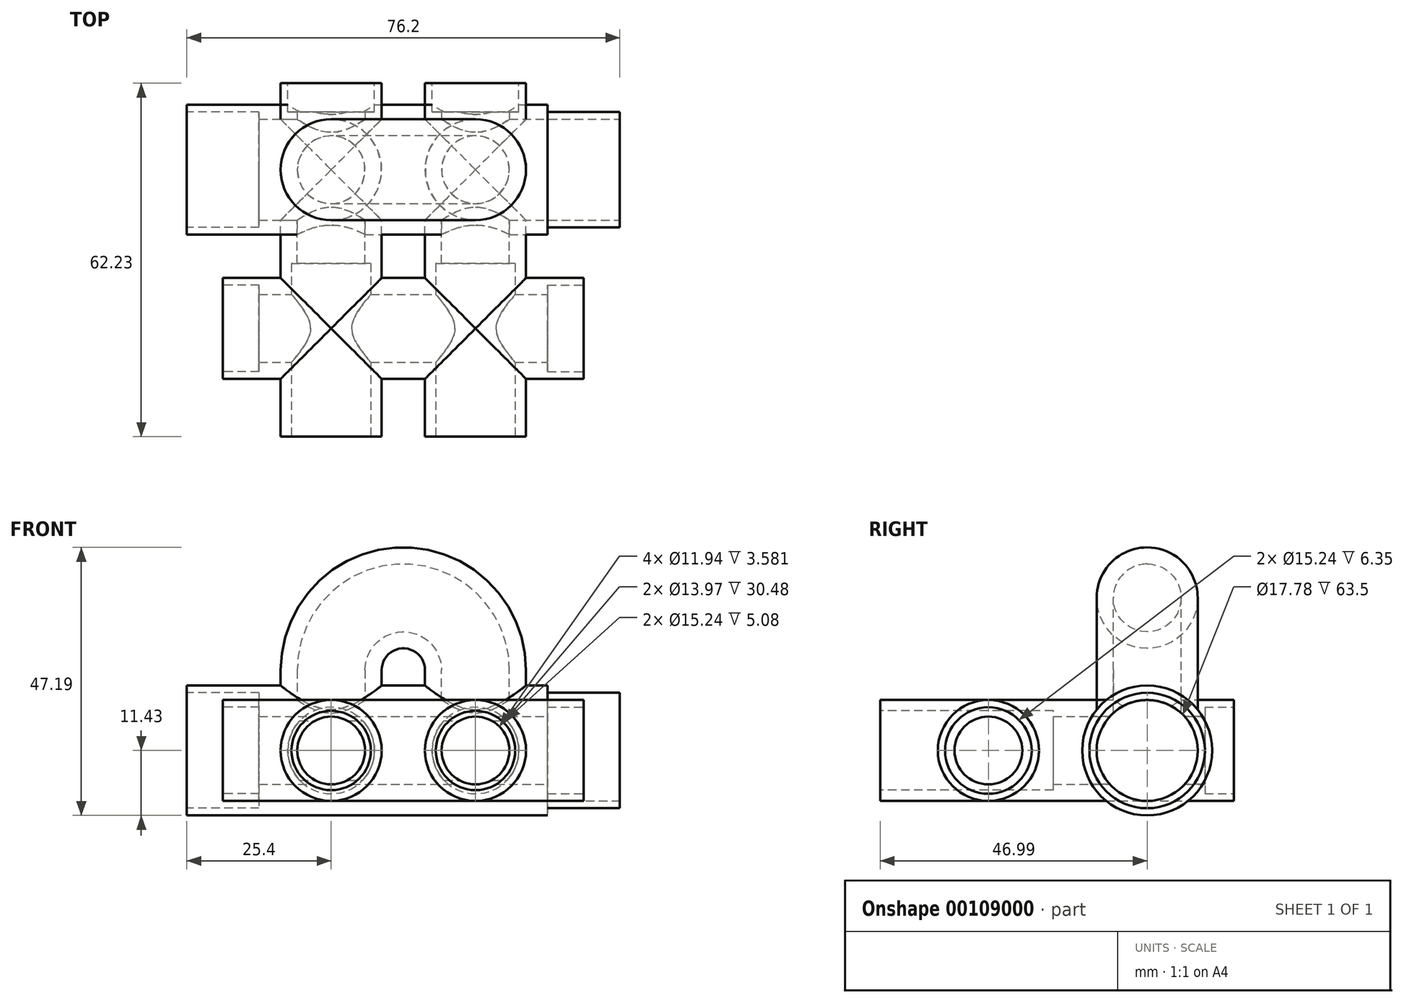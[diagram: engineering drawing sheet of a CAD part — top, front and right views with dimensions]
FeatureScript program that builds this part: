
annotation { "Feature Type Name" : "Feature", "Feature Type Description" : "" }
export const myFeature = defineFeature(function(context is Context, id is Id, definition is map)
    precondition{}
    {
        {
            var Q0;
            Q0=qCreatedBy(makeId("Top.planeOp"),FACE);
            var sketch = newSketch(context, id + "F0", { "sketchPlane" : qUnion([Q0])});
            skLineSegment(sketch, "E0", {"start": v(0, 0) * mm, "end": v(0, 27.94) * mm});
            skLineSegment(sketch, "E1", {"start": v(0, 27.94) * mm, "end": v(-25.4, 27.94) * mm});
            skLineSegment(sketch, "E2", {"start": v(-25.4, 27.94) * mm, "end": v(-25.4, 0) * mm});
            skLineSegment(sketch, "E3", {"start": v(0, 0) * mm, "end": v(0, 43.18) * mm});
            skPoint(sketch, "E3.endSnap0", {"position": v(0, 13.97) * mm});
            skLineSegment(sketch, "E4", {"start": v(-44.94, 0) * mm, "end": v(-34.3, 0) * mm});
            skArc(sketch, "E5", {"start": v(-34.3, 0) * mm, "mid": v(-28, 2.6) * mm, "end": v(-25.4, 8.9) * mm});
            skLineSegment(sketch, "E6", {"start": v(-25.4, 0) * mm, "end": v(0, 0) * mm});
            skLineSegment(sketch, "E7", {"start": v(-34.3, 0) * mm, "end": v(-25.4, 0) * mm});
            skLineSegment(sketch, "E8", {"start": v(-34.3, 0) * mm, "end": v(-34.3, 8.9) * mm});
            skLineSegment(sketch, "E9", {"start": v(-34.3, 8.9) * mm, "end": v(-25.4, 8.9) * mm});
            skSolve(sketch);
        }
        {
            var Q0;
            Q0=qCreatedBy(makeId("Front.planeOp"),FACE);
            var sketch = newSketch(context, id + "F1", { "sketchPlane" : qUnion([Q0])});
            skCircle(sketch, "E10", {"center": v(0, 0) * mm, "radius": 5.97 * mm});
            skCircle(sketch, "E11", {"center": v(0, 0) * mm, "radius": 8.9 * mm});
            skCircle(sketch, "E12", {"center": v(-25.4, 0) * mm, "radius": 5.97 * mm});
            skCircle(sketch, "E13", {"center": v(-25.4, 0) * mm, "radius": 8.9 * mm});
            skSolve(sketch);
        }
        {
            var Q0;
            Q0=qCreatedBy(makeId("Right.planeOp"),FACE);
            cPlane(context, id + "F2", {"entities" : qUnion([Q0]), "cplaneType" : CPlaneType.OFFSET, "offset" : 12.7 * mm, "width" : 152.4 * mm, "height" : 152.4 * mm});
        }
        {
            var Q0;
            Q0=qCreatedBy(id+"F2.planeOp",FACE);
            var sketch = newSketch(context, id + "F3", { "sketchPlane" : qUnion([Q0])});
            skCircle(sketch, "E14", {"center": v(27.94, 0) * mm, "radius": 8.9 * mm});
            skCircle(sketch, "E15", {"center": v(27.94, 0) * mm, "radius": 11.43 * mm});
            skSolve(sketch);
        }
        {
            var Q0;
            Q0=makeQuery(id+"F3.imprint","IMPRINT",FACE,{"disambiguationData":[TD([[makeQuery(id+"F3.imprint","IMPRINT",EDGE,{"derivedFrom":sQuery(id+"F3.wireOp",EDGE,"E14")}),-1.0]])]});
            extrude(context, id + "F4", {"entities" : qUnion([Q0]), "oppositeDirection" : true, "depth" : 63.5 * mm});
        }
        {
            var Q0;
            Q0=qCreatedBy(makeId("Front.planeOp"),FACE);
            cPlane(context, id + "F5", {"entities" : qUnion([Q0]), "cplaneType" : CPlaneType.OFFSET, "offset" : 27.94 * mm, "oppositeDirection" : true, "width" : 152.4 * mm, "height" : 152.4 * mm});
        }
        {
            var Q0;
            Q0=qCreatedBy(id+"F5.planeOp",FACE);
            var sketch = newSketch(context, id + "F6", { "sketchPlane" : qUnion([Q0])});
            skLineSegment(sketch, "E16", {"start": v(0, 0) * mm, "end": v(0, 14.17) * mm});
            skLineSegment(sketch, "E17", {"start": v(-25.4, 0) * mm, "end": v(-25.4, 14.17) * mm});
            skArc(sketch, "E18", {"start": v(-25.4, 14.17) * mm, "mid": v(-12.7, 26.87) * mm, "end": v(0, 14.17) * mm});
            skLineSegment(sketch, "E19", {"start": v(-25.4, 0) * mm, "end": v(-25.4, 8.9) * mm});
            skSolve(sketch);
        }
        {
            var Q0;
            Q0=qCreatedBy(makeId("Top.planeOp"),FACE);
            var sketch = newSketch(context, id + "F7", { "sketchPlane" : qUnion([Q0])});
            skCircle(sketch, "E20", {"center": v(0, 27.94) * mm, "radius": 5.97 * mm});
            skCircle(sketch, "E21", {"center": v(0, 27.94) * mm, "radius": 8.9 * mm});
            skSolve(sketch);
        }
        {
            var Q0;
            Q0=makeQuery(id+"F7.imprint","IMPRINT",FACE,{"disambiguationData":[TD([[makeQuery(id+"F7.imprint","IMPRINT",EDGE,{"derivedFrom":sQuery(id+"F7.wireOp",EDGE,"E20")}),-1.0]])]});
            var Q1;
            Q1=sQuery(id+"F6.wireOp",EDGE,"E16");
            var Q2;
            Q2=sQuery(id+"F6.wireOp",EDGE,"E18");
            var Q3;
            Q3=sQuery(id+"F6.wireOp",EDGE,"E17");
            sweep(context, id + "F8", {"operationType" : NewBodyOperationType.ADD, "profiles" : qUnion([Q0]), "path" : qUnion([Q1, Q2, Q3])});
        }
        {
            var Q0;
            Q0=makeQuery(id+"F1.imprint","IMPRINT",FACE,{"disambiguationData":[TD([[makeQuery(id+"F1.imprint","IMPRINT",EDGE,{"derivedFrom":sQuery(id+"F1.wireOp",EDGE,"E10")}),-1.0]])]});
            var Q1;
            Q1=makeQuery(id+"F1.imprint","IMPRINT",FACE,{"disambiguationData":[TD([[makeQuery(id+"F1.imprint","IMPRINT",EDGE,{"derivedFrom":sQuery(id+"F1.wireOp",EDGE,"E12")}),-1.0]])]});
            var Q2;
            Q2=sQuery(id+"F0.wireOp",EDGE,"E3");
            sweep(context, id + "F9", {"profiles" : qUnion([Q0, Q1]), "path" : qUnion([Q2])});
        }
        {
            var Q0;
            Q0=makeQuery(id+"F3.imprint","IMPRINT",FACE,{"disambiguationData":[TD([[makeQuery(id+"F3.imprint","IMPRINT",EDGE,{"derivedFrom":sQuery(id+"F3.wireOp",EDGE,"E14")}),1.0]])]});
            extrude(context, id + "F10", {"entities" : qUnion([Q0]), "operationType" : NewBodyOperationType.REMOVE, "oppositeDirection" : true, "depth" : 52.65 * mm});
        }
        {
            var Q0;
            Q0=makeQuery(id+"F1.imprint","IMPRINT",FACE,{"disambiguationData":[TD([[makeQuery(id+"F1.imprint","IMPRINT",EDGE,{"derivedFrom":sQuery(id+"F1.wireOp",EDGE,"E12")}),1.0]])]});
            var Q1;
            Q1=makeQuery(id+"F1.imprint","IMPRINT",FACE,{"disambiguationData":[TD([[makeQuery(id+"F1.imprint","IMPRINT",EDGE,{"derivedFrom":sQuery(id+"F1.wireOp",EDGE,"E10")}),1.0]])]});
            extrude(context, id + "F11", {"entities" : qUnion([Q0, Q1]), "operationType" : NewBodyOperationType.REMOVE, "oppositeDirection" : true, "depth" : 69.97 * mm});
        }
        {
            var Q0;
            Q0=makeQuery(id+"F7.imprint","IMPRINT",FACE,{"disambiguationData":[TD([[makeQuery(id+"F7.imprint","IMPRINT",EDGE,{"derivedFrom":sQuery(id+"F7.wireOp",EDGE,"E20")}),1.0]])]});
            var Q1;
            Q1=sQuery(id+"F6.wireOp",EDGE,"E16");
            var Q2;
            Q2=sQuery(id+"F6.wireOp",EDGE,"E18");
            var Q3;
            Q3=sQuery(id+"F6.wireOp",EDGE,"E17");
            sweep(context, id + "F12", {"operationType" : NewBodyOperationType.REMOVE, "profiles" : qUnion([Q0]), "path" : qUnion([Q1, Q2, Q3])});
        }
        {
            var Q0;
            Q0=qCreatedBy(id+"F2.planeOp",FACE);
            var sketch = newSketch(context, id + "F13", { "sketchPlane" : qUnion([Q0])});
            skCircle(sketch, "E22", {"center": v(0, 0) * mm, "radius": 5.97 * mm});
            skCircle(sketch, "E23", {"center": v(0, 0) * mm, "radius": 8.9 * mm});
            skSolve(sketch);
        }
        {
            var Q0;
            Q0=makeQuery(id+"F13.imprint","IMPRINT",FACE,{"disambiguationData":[TD([[makeQuery(id+"F13.imprint","IMPRINT",EDGE,{"derivedFrom":sQuery(id+"F13.wireOp",EDGE,"E22")}),-1.0]])]});
            extrude(context, id + "F14", {"entities" : qUnion([Q0]), "operationType" : NewBodyOperationType.ADD, "oppositeDirection" : true, "depth" : 50.8 * mm});
        }
        {
            var Q0;
            Q0=makeQuery(id+"F1.imprint","IMPRINT",FACE,{"disambiguationData":[TD([[makeQuery(id+"F1.imprint","IMPRINT",EDGE,{"derivedFrom":sQuery(id+"F1.wireOp",EDGE,"E10")}),-1.0]])]});
            var Q1;
            Q1=makeQuery(id+"F1.imprint","IMPRINT",FACE,{"disambiguationData":[TD([[makeQuery(id+"F1.imprint","IMPRINT",EDGE,{"derivedFrom":sQuery(id+"F1.wireOp",EDGE,"E12")}),-1.0]])]});
            extrude(context, id + "F15", {"entities" : qUnion([Q0, Q1]), "operationType" : NewBodyOperationType.ADD, "depth" : 19.05 * mm});
        }
        {
            var Q0;
            Q0=makeQuery(id+"F13.imprint","IMPRINT",FACE,{"disambiguationData":[TD([[makeQuery(id+"F13.imprint","IMPRINT",EDGE,{"derivedFrom":sQuery(id+"F13.wireOp",EDGE,"E22")}),1.0]])]});
            extrude(context, id + "F16", {"entities" : qUnion([Q0]), "operationType" : NewBodyOperationType.REMOVE, "oppositeDirection" : true, "depth" : 50.8 * mm});
        }
        {
            var Q0;
            Q0=makeQuery(id+"F1.imprint","IMPRINT",FACE,{"disambiguationData":[TD([[makeQuery(id+"F1.imprint","IMPRINT",EDGE,{"derivedFrom":sQuery(id+"F1.wireOp",EDGE,"E10")}),1.0]])]});
            extrude(context, id + "F17", {"entities" : qUnion([Q0]), "operationType" : NewBodyOperationType.REMOVE, "depth" : 25.4 * mm});
        }
        {
            var Q0;
            Q0=makeQuery(id+"F1.imprint","IMPRINT",FACE,{"disambiguationData":[TD([[makeQuery(id+"F1.imprint","IMPRINT",EDGE,{"derivedFrom":sQuery(id+"F1.wireOp",EDGE,"E12")}),1.0]])]});
            extrude(context, id + "F18", {"entities" : qUnion([Q0]), "operationType" : NewBodyOperationType.REMOVE, "depth" : 25.4 * mm});
        }
        {
            var Q0;
            Q0=makeQuery(id+"F15.opExtrude","CAP_FACE",FACE,{"disambiguationData":[OSD([sQuery(id+"F1.wireOp",EDGE,"E12"),sQuery(id+"F1.wireOp",EDGE,"E13")])],"isStart":false});
            var sketch = newSketch(context, id + "F19", { "sketchPlane" : qUnion([Q0])});
            skCircle(sketch, "E24", {"center": v(-25.4, 0) * mm, "radius": 6.99 * mm});
            skCircle(sketch, "E25", {"center": v(0, 0) * mm, "radius": 6.99 * mm});
            skSolve(sketch);
        }
        {
            var Q0;
            Q0=makeQuery(id+"F19.imprint","IMPRINT",FACE,{"disambiguationData":[TD([[makeQuery(id+"F19.imprint","IMPRINT",EDGE,{"derivedFrom":sQuery(id+"F19.wireOp",EDGE,"E24")}),1.0]])]});
            extrude(context, id + "F20", {"entities" : qUnion([Q0]), "operationType" : NewBodyOperationType.REMOVE, "oppositeDirection" : true, "depth" : 30.48 * mm});
        }
        {
            var Q0;
            Q0=makeQuery(id+"F19.imprint","IMPRINT",FACE,{"disambiguationData":[TD([[makeQuery(id+"F19.imprint","IMPRINT",EDGE,{"derivedFrom":sQuery(id+"F19.wireOp",EDGE,"E25")}),1.0]])]});
            extrude(context, id + "F21", {"entities" : qUnion([Q0]), "operationType" : NewBodyOperationType.REMOVE, "oppositeDirection" : true, "depth" : 30.48 * mm});
        }
        {
            var Q0;
            Q0=qCreatedBy(id+"F2.planeOp",FACE);
            var sketch = newSketch(context, id + "F22", { "sketchPlane" : qUnion([Q0])});
            skLineSegment(sketch, "E26", {"start": v(5.97, 0) * mm, "end": v(19.05, 0) * mm});
            skSolve(sketch);
        }
        {
            var Q0;
            Q0 = qSketchRegion(id + "F22", true);
            var Q1;
            Q1=makeQuery(id+"F13.imprint","IMPRINT",FACE,{"disambiguationData":[TD([[makeQuery(id+"F13.imprint","IMPRINT",EDGE,{"derivedFrom":sQuery(id+"F13.wireOp",EDGE,"E22")}),-1.0]])]});
            extrude(context, id + "F23", {"entities" : qUnion([Q0, Q1]), "operationType" : NewBodyOperationType.ADD, "depth" : 12.7 * mm});
        }
        {
            var Q0;
            Q0=makeQuery(id+"F14.opExtrude","CAP_FACE",FACE,{"disambiguationData":[OSD([sQuery(id+"F13.wireOp",EDGE,"E22"),sQuery(id+"F13.wireOp",EDGE,"E23")])],"isStart":false});
            extrude(context, id + "F24", {"entities" : qUnion([Q0]), "operationType" : NewBodyOperationType.ADD, "depth" : 12.7 * mm});
        }
        {
            var Q0;
            Q0=makeQuery(id+"F23.opExtrude","CAP_FACE",FACE,{"disambiguationData":[OSD([sQuery(id+"F13.wireOp",EDGE,"E22"),sQuery(id+"F13.wireOp",EDGE,"E23")])],"isStart":false});
            var sketch = newSketch(context, id + "F25", { "sketchPlane" : qUnion([Q0])});
            skCircle(sketch, "E27", {"center": v(0, 0) * mm, "radius": 7.62 * mm});
            skSolve(sketch);
        }
        {
            var Q0;
            Q0=makeQuery(id+"F25.imprint","IMPRINT",FACE,{"disambiguationData":[TD([[makeQuery(id+"F25.imprint","IMPRINT",EDGE,{"derivedFrom":sQuery(id+"F25.wireOp",EDGE,"E27")}),-1.0]])]});
            extrude(context, id + "F26", {"entities" : qUnion([Q0]), "operationType" : NewBodyOperationType.REMOVE, "oppositeDirection" : true, "depth" : 6.35 * mm});
        }
        {
            var Q0;
            Q0=makeQuery(id+"F24.opExtrude","CAP_FACE",FACE,{"disambiguationData":[OSD([sQuery(id+"F13.wireOp",EDGE,"E22"),sQuery(id+"F13.wireOp",EDGE,"E23")])],"isStart":false});
            var sketch = newSketch(context, id + "F27", { "sketchPlane" : qUnion([Q0])});
            skCircle(sketch, "E28", {"center": v(0, 0) * mm, "radius": 7.62 * mm});
            skSolve(sketch);
        }
        {
            var Q0;
            Q0=makeQuery(id+"F19.imprint","IMPRINT",FACE,{"disambiguationData":[TD([[makeQuery(id+"F19.imprint","IMPRINT",EDGE,{"derivedFrom":makeQuery(id+"F15.opExtrude","CAP_EDGE",EDGE,{"disambiguationData":[OSD([sQuery(id+"F1.wireOp",EDGE,"E12")])],"isStart":false})}),1.0]])]});
            extrude(context, id + "F28", {"entities" : qUnion([Q0]), "operationType" : NewBodyOperationType.REMOVE, "oppositeDirection" : true, "depth" : 27.58 * mm});
        }
        {
            var Q0;
            Q0=makeQuery(id+"F27.imprint","IMPRINT",FACE,{"disambiguationData":[TD([[makeQuery(id+"F27.imprint","IMPRINT",EDGE,{"derivedFrom":sQuery(id+"F27.wireOp",EDGE,"E28")}),-1.0]])]});
            extrude(context, id + "F29", {"entities" : qUnion([Q0]), "operationType" : NewBodyOperationType.REMOVE, "oppositeDirection" : true, "depth" : 6.35 * mm});
        }
        {
            var Q0;
            Q0=makeQuery(id+"F19.imprint","IMPRINT",FACE,{"disambiguationData":[TD([[makeQuery(id+"F19.imprint","IMPRINT",EDGE,{"derivedFrom":makeQuery(id+"F15.opExtrude","CAP_EDGE",EDGE,{"disambiguationData":[OSD([sQuery(id+"F1.wireOp",EDGE,"E12")])],"isStart":false})}),1.0]])]});
            extrude(context, id + "F30", {"entities" : qUnion([Q0]), "operationType" : NewBodyOperationType.REMOVE, "oppositeDirection" : true, "depth" : 39.24 * mm});
        }
        {
            var Q0;
            Q0=makeQuery(id+"F9.opSweep","CAP_FACE",FACE,{"disambiguationData":[OSD([sQuery(id+"F0.wireOp",VERTEX,"E3.end"),sQuery(id+"F1.wireOp",EDGE,"E10"),sQuery(id+"F1.wireOp",EDGE,"E11")])],"isStart":false});
            var sketch = newSketch(context, id + "F31", { "sketchPlane" : qUnion([Q0])});
            skCircle(sketch, "E29", {"center": v(0, 0) * mm, "radius": 7.62 * mm});
            skSolve(sketch);
        }
        {
            var Q0;
            Q0=makeQuery(id+"F9.opSweep","CAP_FACE",FACE,{"disambiguationData":[OSD([sQuery(id+"F0.wireOp",VERTEX,"E3.end"),sQuery(id+"F1.wireOp",EDGE,"E12"),sQuery(id+"F1.wireOp",EDGE,"E13")])],"isStart":false});
            var sketch = newSketch(context, id + "F32", { "sketchPlane" : qUnion([Q0])});
            skCircle(sketch, "E30", {"center": v(25.4, 0) * mm, "radius": 7.62 * mm});
            skSolve(sketch);
        }
        {
            var Q0;
            Q0=makeQuery(id+"F31.imprint","IMPRINT",FACE,{"disambiguationData":[TD([[makeQuery(id+"F31.imprint","IMPRINT",EDGE,{"derivedFrom":sQuery(id+"F31.wireOp",EDGE,"E29")}),1.0]])]});
            extrude(context, id + "F33", {"entities" : qUnion([Q0]), "operationType" : NewBodyOperationType.REMOVE, "oppositeDirection" : true, "depth" : 5.08 * mm});
        }
        {
            var Q0;
            Q0=makeQuery(id+"F32.imprint","IMPRINT",FACE,{"disambiguationData":[TD([[makeQuery(id+"F32.imprint","IMPRINT",EDGE,{"derivedFrom":sQuery(id+"F32.wireOp",EDGE,"E30")}),1.0]])]});
            extrude(context, id + "F34", {"entities" : qUnion([Q0]), "operationType" : NewBodyOperationType.REMOVE, "oppositeDirection" : true, "depth" : 5.08 * mm});
        }
        {
            var Q0;
            Q0=qCreatedBy(makeId("Right.planeOp"),FACE);
            var sketch = newSketch(context, id + "F35", { "sketchPlane" : qUnion([Q0])});
            skLineSegment(sketch, "E31", {"start": v(27.94, 0) * mm, "end": v(27.94, -20.32) * mm});
            skSolve(sketch);
        }
        {
            var Q0;
            Q0=makeQuery(id+"F23.opExtrude","CAP_FACE",FACE,{"disambiguationData":[OSD([sQuery(id+"F13.wireOp",EDGE,"E22"),sQuery(id+"F13.wireOp",EDGE,"E23")])],"isStart":false});
            extrude(context, id + "F36", {"entities" : qUnion([Q0]), "operationType" : NewBodyOperationType.REMOVE, "oppositeDirection" : true, "depth" : 12.7 * mm});
        }
        {
            var Q0;
            Q0=makeQuery(id+"F24.opExtrude","CAP_FACE",FACE,{"disambiguationData":[OSD([sQuery(id+"F13.wireOp",EDGE,"E22"),sQuery(id+"F13.wireOp",EDGE,"E23")])],"isStart":false});
            extrude(context, id + "F37", {"entities" : qUnion([Q0]), "operationType" : NewBodyOperationType.REMOVE, "oppositeDirection" : true, "depth" : 12.7 * mm});
        }
        {
            var Q0;
            Q0=makeQuery(id+"F4.opExtrude","CAP_FACE",FACE,{"disambiguationData":[OSD([sQuery(id+"F3.wireOp",EDGE,"E14"),sQuery(id+"F3.wireOp",EDGE,"E15")])],"isStart":false});
            var sketch = newSketch(context, id + "F38", { "sketchPlane" : qUnion([Q0])});
            skCircle(sketch, "E32", {"center": v(-27.94, 0) * mm, "radius": 10.16 * mm});
            skSolve(sketch);
        }
        {
            var Q0;
            Q0=makeQuery(id+"F3.imprint","IMPRINT",FACE,{"disambiguationData":[TD([[makeQuery(id+"F3.imprint","IMPRINT",EDGE,{"derivedFrom":sQuery(id+"F3.wireOp",EDGE,"E14")}),-1.0]])]});
            var sketch = newSketch(context, id + "F39", { "sketchPlane" : qUnion([Q0])});
            skCircle(sketch, "E33", {"center": v(27.94, 0) * mm, "radius": 10.16 * mm});
            skSolve(sketch);
        }
        {
            var Q0;
            Q0=makeQuery(id+"F38.imprint","IMPRINT",FACE,{"disambiguationData":[TD([[makeQuery(id+"F38.imprint","IMPRINT",EDGE,{"derivedFrom":sQuery(id+"F38.wireOp",EDGE,"E32")}),1.0]])]});
            extrude(context, id + "F40", {"entities" : qUnion([Q0]), "operationType" : NewBodyOperationType.REMOVE, "oppositeDirection" : true, "depth" : 12.7 * mm});
        }
        {
            var Q0;
            Q0=makeQuery(id+"F39.imprint","IMPRINT",FACE,{"disambiguationData":[TD([[makeQuery(id+"F39.imprint","IMPRINT",EDGE,{"derivedFrom":sQuery(id+"F39.wireOp",EDGE,"E33")}),1.0]])]});
            extrude(context, id + "F41", {"entities" : qUnion([Q0]), "operationType" : NewBodyOperationType.ADD, "depth" : 12.7 * mm});
        }
    });
